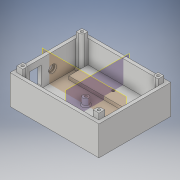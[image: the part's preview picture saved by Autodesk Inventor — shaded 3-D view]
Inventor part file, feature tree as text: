
AUTODESK INVENTOR PART (.ipt)
format: ipt  version: 2019 (Build 230136000, 136)  size: 302,592 bytes
history: native  units: in
note: dims shown in document units (in); Inventor stores cm internally (conversion verified against a paired STEP export)
features: thicken_offset x10, extrude x8, sketch x8, plane x3, chamfer x2, mirror x2, pattern_linear x1
ambient origin geometry x8: Origin, YZ Plane, XZ Plane, XY Plane, X Axis, Y Axis, Z Axis, Center Point
bodies: Solid1 (feature_tree)
feature tree (34):
  extrude  "Extrusion1"  Depth=2.8in
  extrude  "Extrusion2"  Depth=0.14in
  extrude  "Extrusion8"  Depth=0.14in
  pattern_linear  "Rectangular Pattern2"  Spacing1=0.599in  [1 undecoded]
  chamfer  "Chamfer2"  Distance=1.728in
  extrude  "Extrusion9"  Depth=3.01in
  plane  "Work Plane5"
  plane  "Work Plane6"
  extrude  "Extrusion12"  Depth=3.01in
  mirror  "Mirror9"
  mirror  "Mirror10"
  chamfer  "Chamfer3"  Distance=0.3in
  extrude  "Extrusion13"  Depth=3.01in
  thicken_offset  "Thicken1"
  thicken_offset  "Thicken2"
  thicken_offset  "Thicken3"
  thicken_offset  "Thicken4"
  thicken_offset  "Thicken5"
  thicken_offset  "Thicken6"
  thicken_offset  "Thicken7"
  thicken_offset  "Thicken8"
  thicken_offset  "Thicken9"
  thicken_offset  "Thicken10"
  extrude  "Extrusion15"  Depth=3.01in
  extrude  "Extrusion16"  Depth=3.01in TaperAngle=45.0deg
  sketch  "Sketch1"  dims[d0=3.527in d1=2.8in]
  sketch  "Sketch2"  dims[d2=0.14in d3=0.14in]
  sketch  "Sketch8"  dims[d4=0.14in d5=0.14in]
  sketch  "Sketch11"  dims[d6=1.119in d7=0.0in]
  sketch  "Sketch18"  dims[d8=0.14in]
  plane  "Work Plane7"
  sketch  "Sketch22"  dims[d9=0.0in]
  sketch  "Sketch24"  dims[d32=0.101in]
  sketch  "Sketch25"  dims[d33=0.2505in d34=0.599in d35=1.728in d36=0.819in d45=0.254in d46=0.3in d47=0.0in d48=0.7874in d50=1.728in d51=0.7874in d53=-0.819in d57=0.05in d58=0.125in d59=45.0deg d61=3.667in d63=0.247in d64=0.6295in d65=1.4in d66=0.494in d67=0.759in d68=0.7in d69=0.25in d71=1.259in d73=1.0in d74=0.0in d75=3.08in d98=-1.9035in d99=-1.54in d105=0.1185in d106=0.2585in d107=1.369in d108=0.0in d119=0.08in d120=0.125in d121=45.0deg d125=0.34in d126=0.07in d127=0.0in d131=0.008in d132=0.008in d133=0.008in d134=0.008in d135=0.008in d136=0.008in d137=0.008in d138=0.008in d139=0.008in d140=0.008in d141=0.008in d142=0.008in d143=0.008in d144=0.008in d145=0.008in d146=0.008in d147=0.008in d148=0.008in d149=0.008in d150=0.008in d151=2.996in d153=3.01in d155=0.14in d156=0.0in d157=0.112in d158=0.411in d159=1.503in d160=0.172in d161=0.0in d163=3.01in d164=0.828in]
note: 1 required parameter value undecoded (feature->parameter linkage not recoverable at this tier; creation-order binding heuristic only, values carry confidence <= 0.55)
